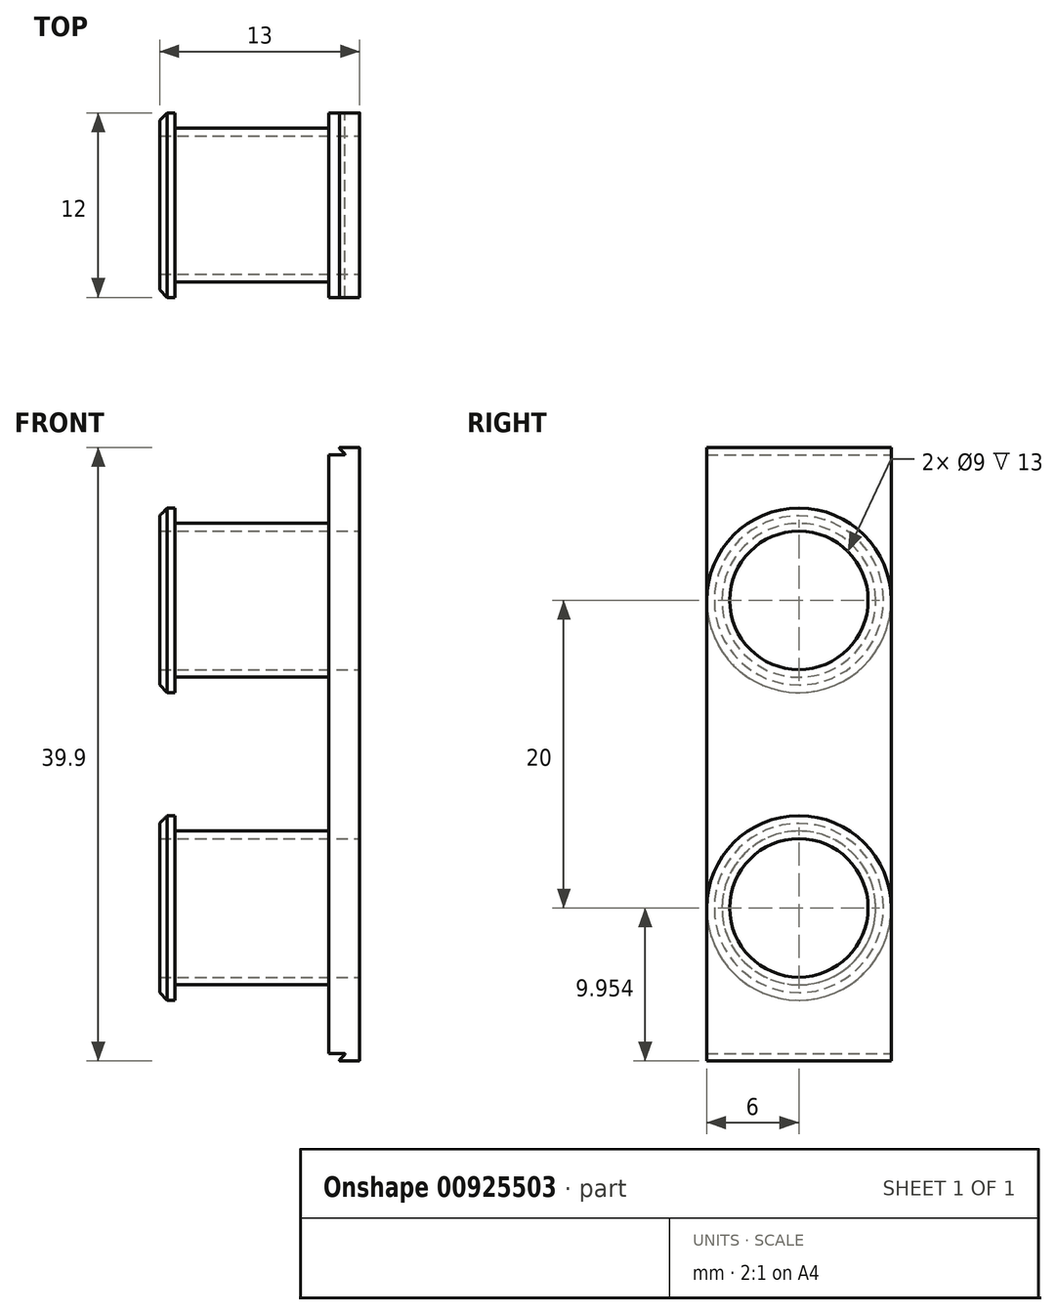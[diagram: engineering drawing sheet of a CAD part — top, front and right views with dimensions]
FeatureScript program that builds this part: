
annotation { "Feature Type Name" : "Feature", "Feature Type Description" : "" }
export const myFeature = defineFeature(function(context is Context, id is Id, definition is map)
    precondition{}
    {
        {
            var Q0;
            Q0=qCreatedBy(makeId("Front.planeOp"),FACE);
            var sketch = newSketch(context, id + "F0", { "sketchPlane" : qUnion([Q0])});
            skLineSegment(sketch, "E0.right", {"start": v(-5.85, 22.43) * mm, "end": v(-5.85, -17.37) * mm});
            skPoint(sketch, "E0.middle", {"position": v(0, 0) * mm});
            skPoint(sketch, "E1.visualSharp", {"position": v(-7.85, -19.47) * mm});
            skLineSegment(sketch, "E2", {"start": v(1.37, 2.53) * mm, "end": v(63.6, 2.53) * mm, "construction": true});
            skLineSegment(sketch, "E3.0", {"start": v(-6.85, 21.98) * mm, "end": v(-7.85, 21.98) * mm});
            skLineSegment(sketch, "E3.1", {"start": v(-7.15, 22.4) * mm, "end": v(-6.82, 22.07) * mm});
            skLineSegment(sketch, "E3.2", {"start": v(-5.9, 22.48) * mm, "end": v(-7.11, 22.48) * mm});
            skLineSegment(sketch, "E4.MirrorCS", {"start": v(-7.15, -17.33) * mm, "end": v(-6.82, -17) * mm});
            skLineSegment(sketch, "E5.MirrorCS", {"start": v(-5.9, -17.42) * mm, "end": v(-7.11, -17.42) * mm});
            skLineSegment(sketch, "E6.MirrorCS", {"start": v(-6.85, -16.92) * mm, "end": v(-7.85, -16.92) * mm});
            skPoint(sketch, "E7.visualSharp", {"position": v(-6.85, 22.03) * mm});
            skLineSegment(sketch, "E8.trimOffspring", {"start": v(-7.85, 21.98) * mm, "end": v(-7.85, -16.92) * mm});
            skArc(sketch, "E9.filletArc", {"start": v(-7.11, 22.48) * mm, "mid": v(-7.16, 22.45) * mm, "end": v(-7.15, 22.4) * mm});
            skPoint(sketch, "E10.visualSharp", {"position": v(-5.85, 22.48) * mm});
            skArc(sketch, "E10.filletArc", {"start": v(-5.85, 22.43) * mm, "mid": v(-5.87, 22.47) * mm, "end": v(-5.9, 22.48) * mm});
            skPoint(sketch, "E11.visualSharp", {"position": v(-7.85, 21.98) * mm});
            skPoint(sketch, "E12.visualSharp", {"position": v(-6.73, 21.98) * mm});
            skArc(sketch, "E12.filletArc", {"start": v(-6.85, 21.98) * mm, "mid": v(-6.8, 22.01) * mm, "end": v(-6.82, 22.07) * mm});
            skArc(sketch, "E13.filletArc", {"start": v(-7.15, -17.33) * mm, "mid": v(-7.16, -17.39) * mm, "end": v(-7.11, -17.42) * mm});
            skPoint(sketch, "E14.visualSharp", {"position": v(-5.85, -17.42) * mm});
            skArc(sketch, "E14.filletArc", {"start": v(-5.9, -17.42) * mm, "mid": v(-5.87, -17.4) * mm, "end": v(-5.85, -17.37) * mm});
            skPoint(sketch, "E15.visualSharp", {"position": v(-6.85, -16.97) * mm});
            skPoint(sketch, "E16.visualSharp", {"position": v(-6.73, -16.92) * mm});
            skArc(sketch, "E16.filletArc", {"start": v(-6.82, -17) * mm, "mid": v(-6.8, -16.95) * mm, "end": v(-6.85, -16.92) * mm});
            skPoint(sketch, "E17", {"position": v(-5.85, 2.53) * mm});
            skSolve(sketch);
        }
        {
            var Q0;
            Q0 = qSketchRegion(id + "F0", true);
            extrude(context, id + "F1", {"entities" : qUnion([Q0]), "depth" : 12 * mm, "offsetDistance" : 25 * mm});
        }
        {
            var Q0;
            Q0=makeQuery(id+"F1.opExtrude","SWEPT_FACE",FACE,{"disambiguationData":[OSD([sQuery(id+"F0.wireOp",EDGE,"E8.trimOffspring")])]});
            var sketch = newSketch(context, id + "F2", { "sketchPlane" : qUnion([Q0])});
            skLineSegment(sketch, "E18", {"start": v(6, 21.98) * mm, "end": v(6, -16.92) * mm, "construction": true});
            skCircle(sketch, "E19", {"center": v(6, 12.53) * mm, "radius": 5 * mm});
            skCircle(sketch, "E20", {"center": v(6, -7.47) * mm, "radius": 5 * mm});
            skPoint(sketch, "E21", {"position": v(6, 2.53) * mm});
            skCircle(sketch, "E22", {"center": v(6, 12.53) * mm, "radius": 4.5 * mm});
            skCircle(sketch, "E23", {"center": v(6, -7.47) * mm, "radius": 4.5 * mm});
            skSolve(sketch);
        }
        {
            var Q0;
            Q0 = qSketchRegion(id + "F2", true);
            extrude(context, id + "F3", {"entities" : qUnion([Q0]), "operationType" : NewBodyOperationType.ADD, "depth" : 10 * mm, "offsetDistance" : 25 * mm});
        }
        {
            var Q0;
            Q0=makeQuery(id+"F3.opExtrude","CAP_FACE",FACE,{"disambiguationData":[OSD([sQuery(id+"F2.wireOp",EDGE,"E19"),sQuery(id+"F2.wireOp",EDGE,"E22")])],"isStart":false});
            var sketch = newSketch(context, id + "F4", { "sketchPlane" : qUnion([Q0])});
            skCircle(sketch, "E24.0", {"center": v(6, 12.53) * mm, "radius": 4.5 * mm});
            skCircle(sketch, "E25.0", {"center": v(6, -7.47) * mm, "radius": 4.5 * mm});
            skCircle(sketch, "E26.0", {"center": v(6, 12.53) * mm, "radius": 6 * mm});
            skCircle(sketch, "E27.0", {"center": v(6, -7.47) * mm, "radius": 6 * mm});
            skSolve(sketch);
        }
        {
            var Q0;
            Q0 = qSketchRegion(id + "F4", true);
            extrude(context, id + "F5", {"entities" : qUnion([Q0]), "operationType" : NewBodyOperationType.ADD, "depth" : 1 * mm, "offsetDistance" : 25 * mm});
        }
        {
            var Q0;
            Q0=makeQuery(id+"F3.boolean.opBoolean","SPLIT",FACE,{"disambiguationData":[TD([makeQuery(id+"F3.opExtrude","SWEPT_FACE",FACE,{"disambiguationData":[OSD([sQuery(id+"F2.wireOp",EDGE,"E22")])]})])],"derivedFrom":makeQuery(id+"F1.opExtrude","SWEPT_FACE",FACE,{"disambiguationData":[OSD([sQuery(id+"F0.wireOp",EDGE,"E8.trimOffspring")])]})});
            var Q1;
            Q1=makeQuery(id+"F3.boolean.opBoolean","SPLIT",FACE,{"disambiguationData":[TD([makeQuery(id+"F3.opExtrude","SWEPT_FACE",FACE,{"disambiguationData":[OSD([sQuery(id+"F2.wireOp",EDGE,"E23")])]})])],"derivedFrom":makeQuery(id+"F1.opExtrude","SWEPT_FACE",FACE,{"disambiguationData":[OSD([sQuery(id+"F0.wireOp",EDGE,"E8.trimOffspring")])]})});
            extrude(context, id + "F6", {"entities" : qUnion([Q0, Q1]), "operationType" : NewBodyOperationType.REMOVE, "oppositeDirection" : true, "depth" : 25 * mm, "offsetDistance" : 25 * mm});
        }
        {
            var Q0;
            Q0=makeQuery(id+"F5.opExtrude","CAP_EDGE",EDGE,{"disambiguationData":[OSD([sQuery(id+"F4.wireOp",EDGE,"E26.0")])],"isStart":false});
            var Q1;
            Q1=makeQuery(id+"F5.opExtrude","CAP_EDGE",EDGE,{"disambiguationData":[OSD([sQuery(id+"F4.wireOp",EDGE,"E27.0")])],"isStart":false});
            chamfer(context, id + "F7", {"entities" : qUnion([Q0, Q1]), "width" : 0.5 * mm, "tangentPropagation" : true});
        }
    });
